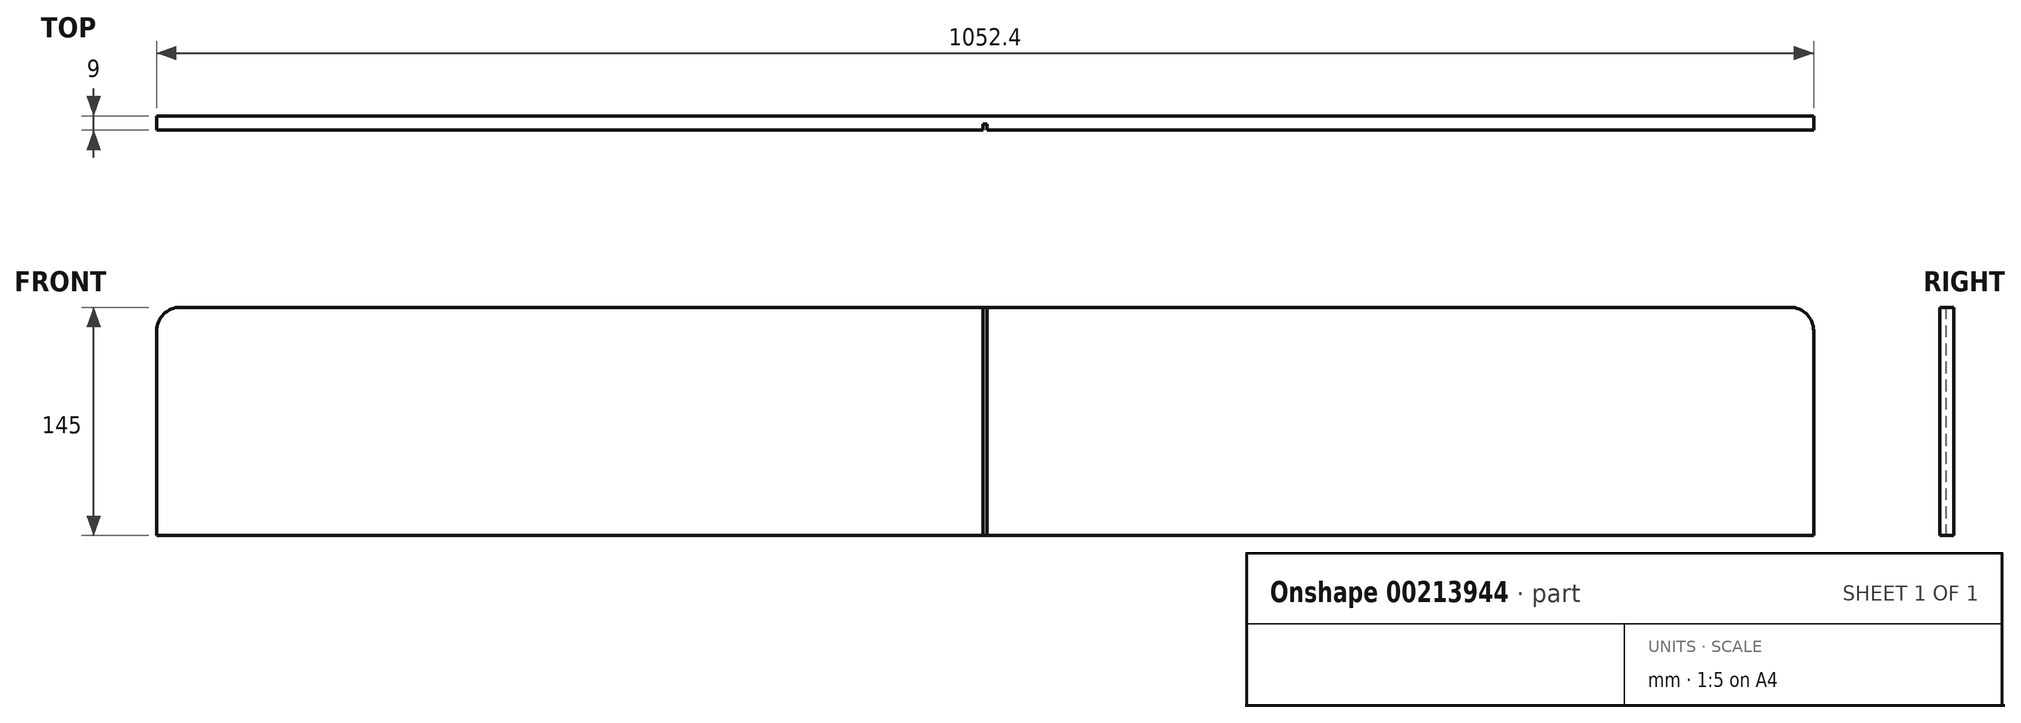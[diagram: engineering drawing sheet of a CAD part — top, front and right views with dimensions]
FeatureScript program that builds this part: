
annotation { "Feature Type Name" : "Feature", "Feature Type Description" : "" }
export const myFeature = defineFeature(function(context is Context, id is Id, definition is map)
    precondition{}
    {
        {
            var Q0;
            Q0=qCreatedBy(makeId("Front.planeOp"),FACE);
            var sketch = newSketch(context, id + "F0", { "sketchPlane" : qUnion([Q0])});
            skLineSegment(sketch, "E0.bottom", {"start": v(1.3, 0) * mm, "end": v(526.2, 0) * mm});
            skLineSegment(sketch, "E0.top", {"start": v(1.3, 145) * mm, "end": v(511.2, 145) * mm});
            skLineSegment(sketch, "E0.left", {"start": v(0, 0) * mm, "end": v(0, 145) * mm, "construction": true});
            skLineSegment(sketch, "E0.right", {"start": v(526.2, 0) * mm, "end": v(526.2, 130) * mm});
            skLineSegment(sketch, "E1", {"start": v(1.3, 145) * mm, "end": v(1.3, 0) * mm});
            skPoint(sketch, "E2.visualSharp", {"position": v(526.2, 145) * mm});
            skArc(sketch, "E2.filletArc", {"start": v(526.2, 130) * mm, "mid": v(521.8, 140.6) * mm, "end": v(511.2, 145) * mm});
            skArc(sketch, "E3.MirrorCS", {"start": v(-526.2, 130) * mm, "mid": v(-521.8, 140.6) * mm, "end": v(-511.2, 145) * mm});
            skPoint(sketch, "E4.MirrorP", {"position": v(-526.2, 145) * mm});
            skLineSegment(sketch, "E5.MirrorCS", {"start": v(-1.3, 0) * mm, "end": v(-526.2, 0) * mm});
            skLineSegment(sketch, "E6.MirrorCS", {"start": v(-526.2, 0) * mm, "end": v(-526.2, 130) * mm});
            skLineSegment(sketch, "E7.MirrorCS", {"start": v(-1.3, 145) * mm, "end": v(-511.2, 145) * mm});
            skLineSegment(sketch, "E8.MirrorCS", {"start": v(-1.3, 145) * mm, "end": v(-1.3, 0) * mm});
            skSolve(sketch);
        }
        {
            var Q0;
            Q0 = qSketchRegion(id + "F0", true);
            extrude(context, id + "F1", {"entities" : qUnion([Q0]), "depth" : 4 * mm});
        }
        {
            var Q0;
            Q0=makeQuery(id+"F1.opExtrude","CAP_FACE",FACE,{"disambiguationData":[OSD([sQuery(id+"F0.wireOp",EDGE,"E3.MirrorCS"),sQuery(id+"F0.wireOp",EDGE,"E5.MirrorCS"),sQuery(id+"F0.wireOp",EDGE,"E6.MirrorCS"),sQuery(id+"F0.wireOp",EDGE,"E7.MirrorCS"),sQuery(id+"F0.wireOp",EDGE,"E8.MirrorCS")])],"isStart":true});
            var sketch = newSketch(context, id + "F2", { "sketchPlane" : qUnion([Q0])});
            skArc(sketch, "E9.0", {"start": v(-526.2, 130) * mm, "mid": v(-521.8, 140.6) * mm, "end": v(-511.2, 145) * mm});
            skLineSegment(sketch, "E9.1", {"start": v(-526.2, 0) * mm, "end": v(-526.2, 130) * mm});
            skArc(sketch, "E9.2", {"start": v(526.2, 130) * mm, "mid": v(521.8, 140.6) * mm, "end": v(511.2, 145) * mm});
            skLineSegment(sketch, "E9.3", {"start": v(526.2, 0) * mm, "end": v(526.2, 130) * mm});
            skLineSegment(sketch, "E10", {"start": v(511.2, 145) * mm, "end": v(-511.2, 145) * mm});
            skLineSegment(sketch, "E11", {"start": v(-526.2, 0) * mm, "end": v(526.2, 0) * mm});
            skSolve(sketch);
        }
        {
            var Q0;
            Q0 = qSketchRegion(id + "F2", true);
            extrude(context, id + "F3", {"entities" : qUnion([Q0]), "operationType" : NewBodyOperationType.ADD, "depth" : 5 * mm});
        }
    });
